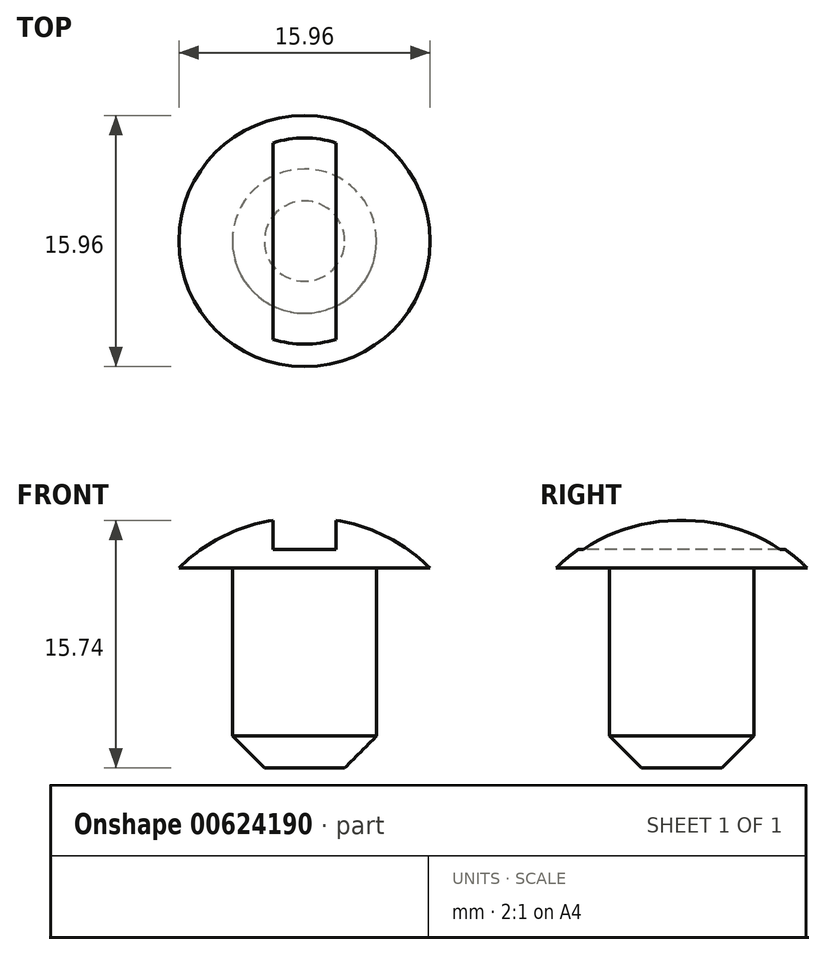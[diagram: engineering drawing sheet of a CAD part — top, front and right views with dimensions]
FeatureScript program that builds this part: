
annotation { "Feature Type Name" : "Feature", "Feature Type Description" : "" }
export const myFeature = defineFeature(function(context is Context, id is Id, definition is map)
    precondition{}
    {
        {
            var Q0;
            Q0=qCreatedBy(makeId("Front.planeOp"),FACE);
            var sketch = newSketch(context, id + "F0", { "sketchPlane" : qUnion([Q0])});
            skLineSegment(sketch, "E0", {"start": v(0, 0) * mm, "end": v(0, 15.88) * mm});
            skLineSegment(sketch, "E1", {"start": v(4.58, 0) * mm, "end": v(4.58, 12.7) * mm});
            skLineSegment(sketch, "E2", {"start": v(4.58, 12.7) * mm, "end": v(7.98, 12.7) * mm});
            skArc(sketch, "E3", {"start": v(7.98, 12.7) * mm, "mid": v(4.31, 15.1) * mm, "end": v(0, 15.88) * mm});
            skLineSegment(sketch, "E4", {"start": v(4.58, 0) * mm, "end": v(0, 0) * mm});
            skSolve(sketch);
        }
        {
            var Q0;
            Q0=makeQuery(id+"F0.imprint","IMPRINT",FACE,{"disambiguationData":[TD([[makeQuery(id+"F0.imprint","IMPRINT",EDGE,{"derivedFrom":sQuery(id+"F0.wireOp",EDGE,"E0")}),-1.0]])]});
            var Q1;
            Q1=sQuery(id+"F0.wireOp",EDGE,"E0");
            revolve(context, id + "F1", {"entities" : qUnion([Q0]), "axis" : qUnion([Q1]), "revolveType" : RevolveType.FULL});
        }
        {
            var Q0;
            Q0=makeQuery(id+"F1.opRevolve","SWEPT_EDGE",EDGE,{"disambiguationData":[OSD([sQuery(id+"F0.wireOp",EDGE,"E1"),sQuery(id+"F0.wireOp",EDGE,"E4")])]});
            chamfer(context, id + "F2", {"entities" : qUnion([Q0]), "width" : 2.03 * mm, "tangentPropagation" : true});
        }
        {
            var Q0;
            Q0=qCreatedBy(makeId("Top.planeOp"),FACE);
            cPlane(context, id + "F3", {"entities" : qUnion([Q0]), "cplaneType" : CPlaneType.OFFSET, "offset" : 28.93 * mm, "width" : 152.4 * mm, "height" : 152.4 * mm});
        }
        {
            var Q0;
            Q0=qCreatedBy(id+"F3.planeOp",FACE);
            var sketch = newSketch(context, id + "F4", { "sketchPlane" : qUnion([Q0])});
            skLineSegment(sketch, "E5.bottom", {"start": v(-2, 10.56) * mm, "end": v(2, 10.56) * mm});
            skLineSegment(sketch, "E5.top", {"start": v(-2, -10.56) * mm, "end": v(2, -10.56) * mm});
            skLineSegment(sketch, "E5.left", {"start": v(-2, 10.56) * mm, "end": v(-2, -10.56) * mm});
            skLineSegment(sketch, "E5.right", {"start": v(2, 10.56) * mm, "end": v(2, -10.56) * mm});
            skPoint(sketch, "E5.middle", {"position": v(0, 0) * mm});
            skSolve(sketch);
        }
        {
            var Q0;
            Q0=makeQuery(id+"F4.imprint","IMPRINT",FACE,{"disambiguationData":[TD([[makeQuery(id+"F4.imprint","IMPRINT",EDGE,{"derivedFrom":sQuery(id+"F4.wireOp",EDGE,"E5.bottom")}),-1.0]])]});
            extrude(context, id + "F5", {"entities" : qUnion([Q0]), "operationType" : NewBodyOperationType.REMOVE, "oppositeDirection" : true, "depth" : 15.04 * mm, "offsetDistance" : 25.4 * mm});
        }
    });
